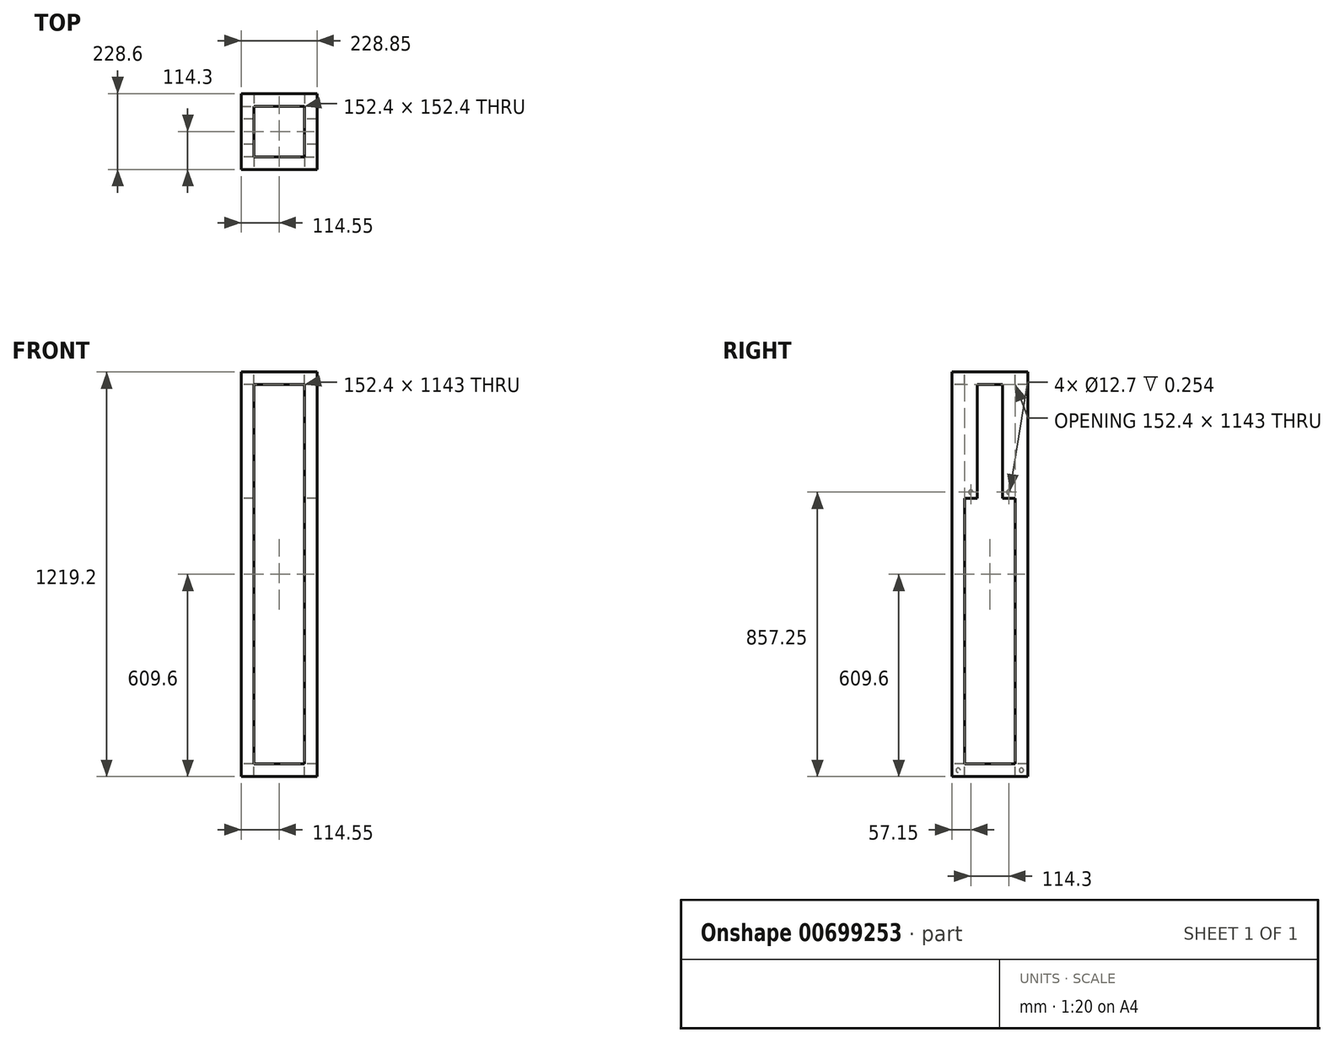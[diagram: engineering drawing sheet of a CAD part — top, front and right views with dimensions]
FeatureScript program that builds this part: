
annotation { "Feature Type Name" : "Feature", "Feature Type Description" : "" }
export const myFeature = defineFeature(function(context is Context, id is Id, definition is map)
    precondition{}
    {
        {
            var Q0;
            Q0=qCreatedBy(makeId("Top.planeOp"),FACE);
            var sketch = newSketch(context, id + "F0", { "sketchPlane" : qUnion([Q0])});
            skLineSegment(sketch, "E0.bottom", {"start": v(114.3, -114.3) * mm, "end": v(-114.3, -114.3) * mm});
            skLineSegment(sketch, "E0.top", {"start": v(114.3, 114.3) * mm, "end": v(-114.3, 114.3) * mm});
            skLineSegment(sketch, "E0.left", {"start": v(114.3, -114.3) * mm, "end": v(114.3, 114.3) * mm});
            skLineSegment(sketch, "E0.right", {"start": v(-114.3, -114.3) * mm, "end": v(-114.3, 114.3) * mm});
            skPoint(sketch, "E0.middle", {"position": v(0, 0) * mm});
            skSolve(sketch);
        }
        {
            var Q0;
            Q0=makeQuery(id+"F0.imprint","IMPRINT",FACE,{"disambiguationData":[TD([[makeQuery(id+"F0.imprint","IMPRINT",EDGE,{"derivedFrom":sQuery(id+"F0.wireOp",EDGE,"E0.bottom")}),-1.0]])]});
            extrude(context, id + "F1", {"entities" : qUnion([Q0]), "oppositeDirection" : true, "depth" : 38.1 * mm, "offsetDistance" : 25.4 * mm});
        }
        {
            var Q0;
            Q0=makeQuery(id+"F1.opExtrude","CAP_FACE",FACE,{"disambiguationData":[OSD([sQuery(id+"F0.wireOp",EDGE,"E0.bottom"),sQuery(id+"F0.wireOp",EDGE,"E0.top"),sQuery(id+"F0.wireOp",EDGE,"E0.left"),sQuery(id+"F0.wireOp",EDGE,"E0.right")])],"isStart":true});
            var sketch = newSketch(context, id + "F2", { "sketchPlane" : qUnion([Q0])});
            skLineSegment(sketch, "E1.bottom", {"start": v(76.2, -76.2) * mm, "end": v(-76.2, -76.2) * mm});
            skLineSegment(sketch, "E1.top", {"start": v(76.2, 76.2) * mm, "end": v(-76.2, 76.2) * mm});
            skLineSegment(sketch, "E1.left", {"start": v(76.2, -76.2) * mm, "end": v(76.2, 76.2) * mm});
            skLineSegment(sketch, "E1.right", {"start": v(-76.2, -76.2) * mm, "end": v(-76.2, 76.2) * mm});
            skPoint(sketch, "E1.middle", {"position": v(0, 0) * mm});
            skSolve(sketch);
        }
        {
            var Q0;
            Q0=makeQuery(id+"F2.imprint","IMPRINT",FACE,{"disambiguationData":[TD([[makeQuery(id+"F2.imprint","IMPRINT",EDGE,{"derivedFrom":sQuery(id+"F2.wireOp",EDGE,"E1.bottom")}),-1.0]])]});
            extrude(context, id + "F3", {"entities" : qUnion([Q0]), "operationType" : NewBodyOperationType.REMOVE, "oppositeDirection" : true, "depth" : 38.1 * mm, "offsetDistance" : 25.4 * mm});
        }
        {
            var Q0;
            Q0=makeQuery(id+"F1.opExtrude","CAP_FACE",FACE,{"disambiguationData":[OSD([sQuery(id+"F0.wireOp",EDGE,"E0.bottom"),sQuery(id+"F0.wireOp",EDGE,"E0.top"),sQuery(id+"F0.wireOp",EDGE,"E0.left"),sQuery(id+"F0.wireOp",EDGE,"E0.right")])],"isStart":true});
            var sketch = newSketch(context, id + "F4", { "sketchPlane" : qUnion([Q0])});
            skLineSegment(sketch, "E2.bottom", {"start": v(-114.3, 114.3) * mm, "end": v(-76.2, 114.3) * mm});
            skLineSegment(sketch, "E2.top", {"start": v(-114.3, 76.2) * mm, "end": v(-76.2, 76.2) * mm});
            skLineSegment(sketch, "E2.left", {"start": v(-114.3, 114.3) * mm, "end": v(-114.3, 76.2) * mm});
            skLineSegment(sketch, "E2.right", {"start": v(-76.2, 114.3) * mm, "end": v(-76.2, 76.2) * mm});
            skLineSegment(sketch, "E3.bottom", {"start": v(114.3, 114.3) * mm, "end": v(76.2, 114.3) * mm});
            skLineSegment(sketch, "E3.top", {"start": v(114.3, 76.2) * mm, "end": v(76.2, 76.2) * mm});
            skLineSegment(sketch, "E3.left", {"start": v(114.3, 114.3) * mm, "end": v(114.3, 76.2) * mm});
            skLineSegment(sketch, "E3.right", {"start": v(76.2, 114.3) * mm, "end": v(76.2, 76.2) * mm});
            skLineSegment(sketch, "E4.bottom", {"start": v(76.2, -76.2) * mm, "end": v(114.3, -76.2) * mm});
            skLineSegment(sketch, "E4.top", {"start": v(76.2, -114.3) * mm, "end": v(114.3, -114.3) * mm});
            skLineSegment(sketch, "E4.left", {"start": v(76.2, -76.2) * mm, "end": v(76.2, -114.3) * mm});
            skLineSegment(sketch, "E4.right", {"start": v(114.3, -76.2) * mm, "end": v(114.3, -114.3) * mm});
            skLineSegment(sketch, "E5.bottom", {"start": v(-76.2, -76.2) * mm, "end": v(-114.3, -76.2) * mm});
            skLineSegment(sketch, "E5.top", {"start": v(-76.2, -114.3) * mm, "end": v(-114.3, -114.3) * mm});
            skLineSegment(sketch, "E5.left", {"start": v(-76.2, -76.2) * mm, "end": v(-76.2, -114.3) * mm});
            skLineSegment(sketch, "E5.right", {"start": v(-114.3, -76.2) * mm, "end": v(-114.3, -114.3) * mm});
            skSolve(sketch);
        }
        {
            var Q0;
            Q0 = qSketchRegion(id + "F4", true);
            extrude(context, id + "F5", {"entities" : qUnion([Q0]), "operationType" : NewBodyOperationType.ADD, "depth" : 1143 * mm, "offsetDistance" : 25.4 * mm});
        }
        {
            var Q0;
            Q0=makeQuery(id+"F5.opExtrude","CAP_FACE",FACE,{"disambiguationData":[OSD([sQuery(id+"F4.wireOp",EDGE,"E2.bottom"),sQuery(id+"F4.wireOp",EDGE,"E2.top"),sQuery(id+"F4.wireOp",EDGE,"E2.left"),sQuery(id+"F4.wireOp",EDGE,"E2.right")])],"isStart":false});
            var sketch = newSketch(context, id + "F6", { "sketchPlane" : qUnion([Q0])});
            skLineSegment(sketch, "E6.bottom", {"start": v(-114.3, 114.3) * mm, "end": v(114.3, 114.3) * mm});
            skLineSegment(sketch, "E6.top", {"start": v(-114.3, -114.3) * mm, "end": v(114.3, -114.3) * mm});
            skLineSegment(sketch, "E6.left", {"start": v(-114.3, 114.3) * mm, "end": v(-114.3, -114.3) * mm});
            skLineSegment(sketch, "E6.right", {"start": v(114.3, 114.3) * mm, "end": v(114.3, -114.3) * mm});
            skSolve(sketch);
        }
        {
            var Q0;
            Q0 = qSketchRegion(id + "F6", true);
            extrude(context, id + "F7", {"entities" : qUnion([Q0]), "operationType" : NewBodyOperationType.ADD, "depth" : 38.1 * mm, "offsetDistance" : 25.4 * mm});
        }
        {
            var Q0;
            Q0=makeQuery(id+"F7.opExtrude","CAP_FACE",FACE,{"disambiguationData":[OSD([sQuery(id+"F6.wireOp",EDGE,"E6.bottom"),sQuery(id+"F6.wireOp",EDGE,"E6.top"),sQuery(id+"F6.wireOp",EDGE,"E6.left"),sQuery(id+"F6.wireOp",EDGE,"E6.right")])],"isStart":false});
            var sketch = newSketch(context, id + "F8", { "sketchPlane" : qUnion([Q0])});
            skLineSegment(sketch, "E7.bottom", {"start": v(76.2, -76.2) * mm, "end": v(-76.2, -76.2) * mm});
            skLineSegment(sketch, "E7.top", {"start": v(76.2, 76.2) * mm, "end": v(-76.2, 76.2) * mm});
            skLineSegment(sketch, "E7.left", {"start": v(76.2, -76.2) * mm, "end": v(76.2, 76.2) * mm});
            skLineSegment(sketch, "E7.right", {"start": v(-76.2, -76.2) * mm, "end": v(-76.2, 76.2) * mm});
            skPoint(sketch, "E7.middle", {"position": v(0, 0) * mm});
            skSolve(sketch);
        }
        {
            var Q0;
            Q0 = qSketchRegion(id + "F8", true);
            extrude(context, id + "F9", {"entities" : qUnion([Q0]), "operationType" : NewBodyOperationType.REMOVE, "oppositeDirection" : true, "depth" : 38.1 * mm, "offsetDistance" : 25.4 * mm});
        }
        {
            var Q0;
            {var subQ0=sQuery(id+"F6.wireOp",EDGE,"E6.right");var subQ1=makeQuery(id+"F7.opExtrude","CAP_FACE",FACE,{"disambiguationData":[OSD([sQuery(id+"F6.wireOp",EDGE,"E6.bottom"),sQuery(id+"F6.wireOp",EDGE,"E6.top"),sQuery(id+"F6.wireOp",EDGE,"E6.left"),subQ0])],"isStart":true});Q0=makeQuery(id+"F9.boolean.opBoolean","SPLIT",FACE,{"disambiguationData":[TD([makeQuery(id+"F1.opExtrude","SWEPT_FACE",FACE,{"disambiguationData":[OSD([sQuery(id+"F0.wireOp",EDGE,"E0.left")])]})])],"derivedFrom":subQ1});}
            var sketch = newSketch(context, id + "F10", { "sketchPlane" : qUnion([Q0])});
            skLineSegment(sketch, "E8.bottom", {"start": v(114.3, 76.2) * mm, "end": v(76.2, 76.2) * mm});
            skLineSegment(sketch, "E8.top", {"start": v(114.3, 38.1) * mm, "end": v(76.2, 38.1) * mm});
            skLineSegment(sketch, "E8.left", {"start": v(114.3, 76.2) * mm, "end": v(114.3, 38.1) * mm});
            skLineSegment(sketch, "E8.right", {"start": v(76.2, 76.2) * mm, "end": v(76.2, 38.1) * mm});
            skLineSegment(sketch, "E9.bottom", {"start": v(114.3, -76.2) * mm, "end": v(76.2, -76.2) * mm});
            skLineSegment(sketch, "E9.top", {"start": v(114.3, -38.1) * mm, "end": v(76.2, -38.1) * mm});
            skLineSegment(sketch, "E9.left", {"start": v(114.3, -76.2) * mm, "end": v(114.3, -38.1) * mm});
            skLineSegment(sketch, "E9.right", {"start": v(76.2, -76.2) * mm, "end": v(76.2, -38.1) * mm});
            skSolve(sketch);
        }
        {
            var Q0;
            Q0 = qSketchRegion(id + "F10", true);
            extrude(context, id + "F11", {"entities" : qUnion([Q0]), "operationType" : NewBodyOperationType.ADD, "depth" : 342.9 * mm, "offsetDistance" : 25.4 * mm});
        }
        {
            var Q0;
            {var subQ0=sQuery(id+"F6.wireOp",EDGE,"E6.left");var subQ1=makeQuery(id+"F7.opExtrude","CAP_FACE",FACE,{"disambiguationData":[OSD([sQuery(id+"F6.wireOp",EDGE,"E6.bottom"),sQuery(id+"F6.wireOp",EDGE,"E6.top"),subQ0,sQuery(id+"F6.wireOp",EDGE,"E6.right")])],"isStart":true});Q0=makeQuery(id+"F9.boolean.opBoolean","SPLIT",FACE,{"disambiguationData":[TD([makeQuery(id+"F1.opExtrude","SWEPT_FACE",FACE,{"disambiguationData":[OSD([sQuery(id+"F0.wireOp",EDGE,"E0.right")])]})])],"derivedFrom":subQ1});}
            var sketch = newSketch(context, id + "F12", { "sketchPlane" : qUnion([Q0])});
            skLineSegment(sketch, "E10.bottom", {"start": v(-76.2, -76.2) * mm, "end": v(-114.3, -76.2) * mm});
            skLineSegment(sketch, "E10.top", {"start": v(-76.2, -38.1) * mm, "end": v(-114.3, -38.1) * mm});
            skLineSegment(sketch, "E10.left", {"start": v(-76.2, -76.2) * mm, "end": v(-76.2, -38.1) * mm});
            skLineSegment(sketch, "E10.right", {"start": v(-114.3, -76.2) * mm, "end": v(-114.3, -38.1) * mm});
            skLineSegment(sketch, "E11.bottom", {"start": v(-76.2, 76.2) * mm, "end": v(-114.3, 76.2) * mm});
            skLineSegment(sketch, "E11.top", {"start": v(-76.2, 38.1) * mm, "end": v(-114.3, 38.1) * mm});
            skLineSegment(sketch, "E11.left", {"start": v(-76.2, 76.2) * mm, "end": v(-76.2, 38.1) * mm});
            skLineSegment(sketch, "E11.right", {"start": v(-114.3, 76.2) * mm, "end": v(-114.3, 38.1) * mm});
            skSolve(sketch);
        }
        {
            var Q0;
            Q0 = qSketchRegion(id + "F12", true);
            extrude(context, id + "F13", {"entities" : qUnion([Q0]), "operationType" : NewBodyOperationType.ADD, "depth" : 342.9 * mm, "offsetDistance" : 25.4 * mm});
        }
        {
            var Q0;
            Q0=makeQuery(id+"F13.boolean.opBoolean","MERGE",FACE,{"derivedFrom":[makeQuery(id+"F7.boolean.opBoolean","MERGE",FACE,{"derivedFrom":[makeQuery(id+"F5.boolean.opBoolean","MERGE",FACE,{"derivedFrom":[makeQuery(id+"F1.opExtrude","SWEPT_FACE",FACE,{"disambiguationData":[OSD([sQuery(id+"F0.wireOp",EDGE,"E0.right")])]}),makeQuery(id+"F5.opExtrude","SWEPT_FACE",FACE,{"disambiguationData":[OSD([sQuery(id+"F4.wireOp",EDGE,"E2.left")])]}),makeQuery(id+"F5.opExtrude","SWEPT_FACE",FACE,{"disambiguationData":[OSD([sQuery(id+"F4.wireOp",EDGE,"E5.right")])]})]}),makeQuery(id+"F7.opExtrude","SWEPT_FACE",FACE,{"disambiguationData":[OSD([sQuery(id+"F6.wireOp",EDGE,"E6.left")])]})]}),makeQuery(id+"F13.opExtrude","SWEPT_FACE",FACE,{"disambiguationData":[OSD([sQuery(id+"F12.wireOp",EDGE,"E10.right")])]}),makeQuery(id+"F13.opExtrude","SWEPT_FACE",FACE,{"disambiguationData":[OSD([sQuery(id+"F12.wireOp",EDGE,"E11.right")])]})]});
            var sketch = newSketch(context, id + "F14", { "sketchPlane" : qUnion([Q0])});
            skLineSegment(sketch, "E12.bottom", {"start": v(76.2, 0) * mm, "end": v(114.3, 0) * mm});
            skLineSegment(sketch, "E12.top", {"start": v(76.2, -38.1) * mm, "end": v(114.3, -38.1) * mm});
            skLineSegment(sketch, "E12.left", {"start": v(76.2, 0) * mm, "end": v(76.2, -38.1) * mm});
            skLineSegment(sketch, "E12.right", {"start": v(114.3, 0) * mm, "end": v(114.3, -38.1) * mm});
            skCircle(sketch, "E13", {"center": v(95.25, -19.05) * mm, "radius": 6.35 * mm});
            skPoint(sketch, "E13.centerSnap0", {"position": v(76.2, -19.05) * mm});
            skPoint(sketch, "E13.centerSnap1", {"position": v(95.25, -38.1) * mm});
            skLineSegment(sketch, "E14.bottom", {"start": v(-114.3, -38.1) * mm, "end": v(-76.2, -38.1) * mm});
            skLineSegment(sketch, "E14.top", {"start": v(-114.3, 0) * mm, "end": v(-76.2, 0) * mm});
            skLineSegment(sketch, "E14.left", {"start": v(-114.3, -38.1) * mm, "end": v(-114.3, 0) * mm});
            skLineSegment(sketch, "E14.right", {"start": v(-76.2, -38.1) * mm, "end": v(-76.2, 0) * mm});
            skCircle(sketch, "E15", {"center": v(-95.25, -19.05) * mm, "radius": 6.35 * mm});
            skPoint(sketch, "E15.centerSnap0", {"position": v(-76.2, -19.05) * mm});
            skPoint(sketch, "E15.centerSnap1", {"position": v(-95.25, 0) * mm});
            skSolve(sketch);
        }
        {
            var Q0;
            Q0=makeQuery(id+"F14.imprint","IMPRINT",FACE,{"disambiguationData":[TD([[makeQuery(id+"F14.imprint","IMPRINT",EDGE,{"derivedFrom":sQuery(id+"F14.wireOp",EDGE,"E15")}),1.0]])]});
            var Q1;
            Q1=makeQuery(id+"F14.imprint","IMPRINT",FACE,{"disambiguationData":[TD([[makeQuery(id+"F14.imprint","IMPRINT",EDGE,{"derivedFrom":sQuery(id+"F14.wireOp",EDGE,"E13")}),1.0]])]});
            extrude(context, id + "F15", {"entities" : qUnion([Q0, Q1]), "operationType" : NewBodyOperationType.ADD, "depth" : 0.25 * mm, "offsetDistance" : 25.4 * mm});
        }
        {
            var Q0;
            Q0=makeQuery(id+"F13.boolean.opBoolean","MERGE",FACE,{"derivedFrom":[makeQuery(id+"F5.opExtrude","SWEPT_FACE",FACE,{"disambiguationData":[OSD([sQuery(id+"F4.wireOp",EDGE,"E2.right")])]}),makeQuery(id+"F5.opExtrude","SWEPT_FACE",FACE,{"disambiguationData":[OSD([sQuery(id+"F4.wireOp",EDGE,"E5.left")])]}),makeQuery(id+"F9.boolean.opBoolean","COPY",FACE,{"derivedFrom":makeQuery(id+"F9.opExtrude","SWEPT_FACE",FACE,{"disambiguationData":[OSD([sQuery(id+"F8.wireOp",EDGE,"E7.right")])]})}),makeQuery(id+"F13.opExtrude","SWEPT_FACE",FACE,{"disambiguationData":[OSD([sQuery(id+"F12.wireOp",EDGE,"E10.left")])]}),makeQuery(id+"F13.opExtrude","SWEPT_FACE",FACE,{"disambiguationData":[OSD([sQuery(id+"F12.wireOp",EDGE,"E11.left")])]})]});
            var sketch = newSketch(context, id + "F16", { "sketchPlane" : qUnion([Q0])});
            skLineSegment(sketch, "E16.bottom", {"start": v(76.2, 800.1) * mm, "end": v(38.1, 800.1) * mm});
            skLineSegment(sketch, "E16.top", {"start": v(76.2, 838.2) * mm, "end": v(38.1, 838.2) * mm});
            skLineSegment(sketch, "E16.left", {"start": v(76.2, 800.1) * mm, "end": v(76.2, 838.2) * mm});
            skLineSegment(sketch, "E16.right", {"start": v(38.1, 800.1) * mm, "end": v(38.1, 838.2) * mm});
            skLineSegment(sketch, "E17.bottom", {"start": v(-76.2, 800.1) * mm, "end": v(-38.1, 800.1) * mm});
            skLineSegment(sketch, "E17.top", {"start": v(-76.2, 838.2) * mm, "end": v(-38.1, 838.2) * mm});
            skLineSegment(sketch, "E17.left", {"start": v(-76.2, 800.1) * mm, "end": v(-76.2, 838.2) * mm});
            skLineSegment(sketch, "E17.right", {"start": v(-38.1, 800.1) * mm, "end": v(-38.1, 838.2) * mm});
            skCircle(sketch, "E18", {"center": v(-57.15, 819.15) * mm, "radius": 6.35 * mm});
            skPoint(sketch, "E18.centerSnap0", {"position": v(-38.1, 819.15) * mm});
            skPoint(sketch, "E18.centerSnap1", {"position": v(-57.15, 800.1) * mm});
            skCircle(sketch, "E19", {"center": v(57.15, 819.15) * mm, "radius": 6.35 * mm});
            skPoint(sketch, "E19.centerSnap0", {"position": v(38.1, 819.15) * mm});
            skPoint(sketch, "E19.centerSnap1", {"position": v(57.15, 800.1) * mm});
            skSolve(sketch);
        }
        {
            var Q0;
            Q0=makeQuery(id+"F16.imprint","IMPRINT",FACE,{"disambiguationData":[TD([[makeQuery(id+"F16.imprint","IMPRINT",EDGE,{"derivedFrom":sQuery(id+"F16.wireOp",EDGE,"E18")}),1.0]])]});
            var Q1;
            Q1=makeQuery(id+"F16.imprint","IMPRINT",FACE,{"disambiguationData":[TD([[makeQuery(id+"F16.imprint","IMPRINT",EDGE,{"derivedFrom":sQuery(id+"F16.wireOp",EDGE,"E19")}),1.0]])]});
            extrude(context, id + "F17", {"entities" : qUnion([Q0, Q1]), "operationType" : NewBodyOperationType.REMOVE, "oppositeDirection" : true, "depth" : 0.25 * mm, "offsetDistance" : 25.4 * mm});
        }
        {
            var Q0;
            Q0=makeQuery(id+"F11.boolean.opBoolean","MERGE",FACE,{"derivedFrom":[makeQuery(id+"F5.opExtrude","SWEPT_FACE",FACE,{"disambiguationData":[OSD([sQuery(id+"F4.wireOp",EDGE,"E3.right")])]}),makeQuery(id+"F5.opExtrude","SWEPT_FACE",FACE,{"disambiguationData":[OSD([sQuery(id+"F4.wireOp",EDGE,"E4.left")])]}),makeQuery(id+"F9.boolean.opBoolean","COPY",FACE,{"derivedFrom":makeQuery(id+"F9.opExtrude","SWEPT_FACE",FACE,{"disambiguationData":[OSD([sQuery(id+"F8.wireOp",EDGE,"E7.left")])]})}),makeQuery(id+"F11.opExtrude","SWEPT_FACE",FACE,{"disambiguationData":[OSD([sQuery(id+"F10.wireOp",EDGE,"E8.right")])]}),makeQuery(id+"F11.opExtrude","SWEPT_FACE",FACE,{"disambiguationData":[OSD([sQuery(id+"F10.wireOp",EDGE,"E9.right")])]})]});
            var sketch = newSketch(context, id + "F18", { "sketchPlane" : qUnion([Q0])});
            skLineSegment(sketch, "E20.bottom", {"start": v(-76.2, 800.1) * mm, "end": v(-38.1, 800.1) * mm});
            skLineSegment(sketch, "E20.top", {"start": v(-76.2, 838.2) * mm, "end": v(-38.1, 838.2) * mm});
            skLineSegment(sketch, "E20.left", {"start": v(-76.2, 800.1) * mm, "end": v(-76.2, 838.2) * mm});
            skLineSegment(sketch, "E20.right", {"start": v(-38.1, 800.1) * mm, "end": v(-38.1, 838.2) * mm});
            skLineSegment(sketch, "E21.bottom", {"start": v(76.2, 800.1) * mm, "end": v(38.1, 800.1) * mm});
            skLineSegment(sketch, "E21.top", {"start": v(76.2, 838.2) * mm, "end": v(38.1, 838.2) * mm});
            skLineSegment(sketch, "E21.left", {"start": v(76.2, 800.1) * mm, "end": v(76.2, 838.2) * mm});
            skLineSegment(sketch, "E21.right", {"start": v(38.1, 800.1) * mm, "end": v(38.1, 838.2) * mm});
            skCircle(sketch, "E22", {"center": v(57.15, 819.15) * mm, "radius": 6.35 * mm});
            skPoint(sketch, "E22.centerSnap0", {"position": v(57.15, 800.1) * mm});
            skPoint(sketch, "E22.centerSnap1", {"position": v(38.1, 819.15) * mm});
            skCircle(sketch, "E23", {"center": v(-57.15, 819.15) * mm, "radius": 6.35 * mm});
            skPoint(sketch, "E23.centerSnap0", {"position": v(-38.1, 819.15) * mm});
            skPoint(sketch, "E23.centerSnap1", {"position": v(-57.15, 800.1) * mm});
            skSolve(sketch);
        }
        {
            var Q0;
            Q0=makeQuery(id+"F18.imprint","IMPRINT",FACE,{"disambiguationData":[TD([[makeQuery(id+"F18.imprint","IMPRINT",EDGE,{"derivedFrom":sQuery(id+"F18.wireOp",EDGE,"E23")}),1.0]])]});
            var Q1;
            Q1=makeQuery(id+"F18.imprint","IMPRINT",FACE,{"disambiguationData":[TD([[makeQuery(id+"F18.imprint","IMPRINT",EDGE,{"derivedFrom":sQuery(id+"F18.wireOp",EDGE,"E22")}),1.0]])]});
            extrude(context, id + "F19", {"entities" : qUnion([Q0, Q1]), "operationType" : NewBodyOperationType.REMOVE, "oppositeDirection" : true, "depth" : 0.25 * mm, "offsetDistance" : 25.4 * mm});
        }
    });
